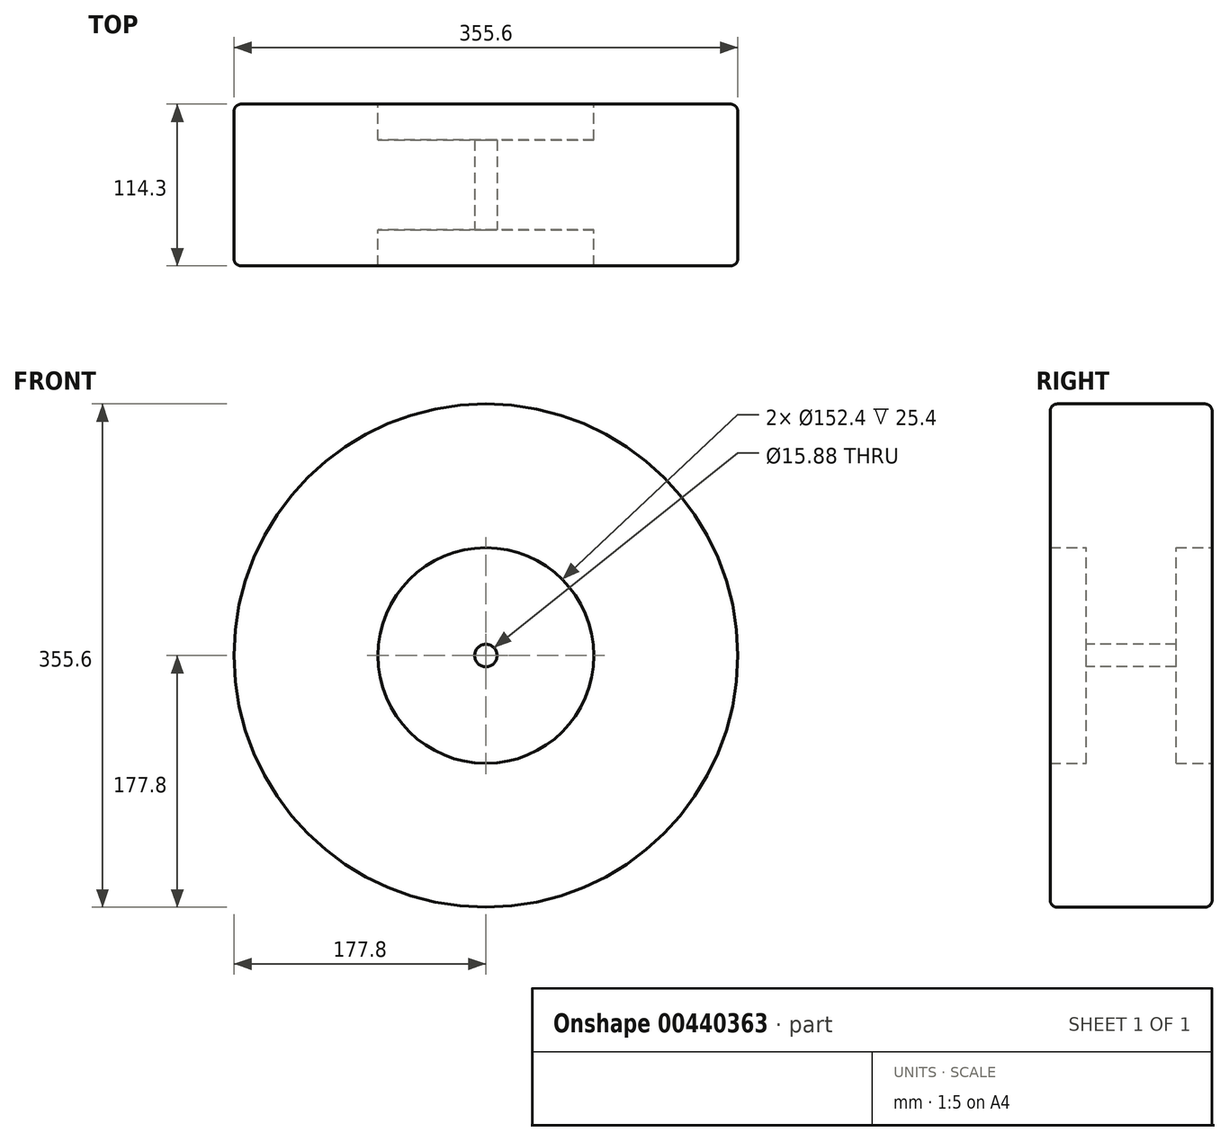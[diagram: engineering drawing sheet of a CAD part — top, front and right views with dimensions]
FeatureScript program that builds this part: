
annotation { "Feature Type Name" : "Feature", "Feature Type Description" : "" }
export const myFeature = defineFeature(function(context is Context, id is Id, definition is map)
    precondition{}
    {
        {
            var Q0;
            Q0=qCreatedBy(makeId("Front.planeOp"),FACE);
            var sketch = newSketch(context, id + "F0", { "sketchPlane" : qUnion([Q0])});
            skCircle(sketch, "E0", {"center": v(0, 0) * mm, "radius": 177.8 * mm});
            skCircle(sketch, "E1", {"center": v(0, 0) * mm, "radius": 76.2 * mm});
            skCircle(sketch, "E2", {"center": v(0, 0) * mm, "radius": 7.94 * mm});
            skSolve(sketch);
        }
        {
            var Q0;
            Q0=makeQuery(id+"F0.imprint","IMPRINT",FACE,{"disambiguationData":[TD([[makeQuery(id+"F0.imprint","IMPRINT",EDGE,{"derivedFrom":sQuery(id+"F0.wireOp",EDGE,"E0")}),1.0]])]});
            extrude(context, id + "F1", {"entities" : qUnion([Q0]), "endBound" : BoundingType.SYMMETRIC, "depth" : 114.3 * mm});
        }
        {
            var Q0;
            Q0=qCreatedBy(makeId("Front.planeOp"),FACE);
            var sketch = newSketch(context, id + "F2", { "sketchPlane" : qUnion([Q0])});
            skCircle(sketch, "E3", {"center": v(0, 0) * mm, "radius": 76.2 * mm});
            skSolve(sketch);
        }
        {
            var Q0;
            Q0=makeQuery(id+"F2.imprint","IMPRINT",FACE,{"disambiguationData":[TD([[makeQuery(id+"F2.imprint","IMPRINT",EDGE,{"derivedFrom":sQuery(id+"F2.wireOp",EDGE,"E3")}),1.0]])]});
            extrude(context, id + "F3", {"entities" : qUnion([Q0]), "operationType" : NewBodyOperationType.ADD, "endBound" : BoundingType.SYMMETRIC, "depth" : 63.5 * mm});
        }
        {
            var Q0;
            Q0=makeQuery(id+"F3.opExtrude","CAP_FACE",FACE,{"disambiguationData":[OSD([sQuery(id+"F2.wireOp",EDGE,"E3")])],"isStart":false});
            var sketch = newSketch(context, id + "F4", { "sketchPlane" : qUnion([Q0])});
            skCircle(sketch, "E4", {"center": v(0, 0) * mm, "radius": 7.94 * mm});
            skSolve(sketch);
        }
        {
            var Q0;
            Q0=makeQuery(id+"F4.imprint","IMPRINT",FACE,{"disambiguationData":[TD([[makeQuery(id+"F4.imprint","IMPRINT",EDGE,{"derivedFrom":sQuery(id+"F4.wireOp",EDGE,"E4")}),1.0]])]});
            extrude(context, id + "F5", {"entities" : qUnion([Q0]), "operationType" : NewBodyOperationType.REMOVE, "endBound" : BoundingType.SYMMETRIC, "oppositeDirection" : true, "depth" : 127 * mm});
        }
        {
            var Q0;
            Q0=makeQuery(id+"F1.opExtrude","CAP_EDGE",EDGE,{"disambiguationData":[OSD([sQuery(id+"F0.wireOp",EDGE,"E0")])],"isStart":false});
            var Q1;
            Q1=makeQuery(id+"F1.opExtrude","CAP_EDGE",EDGE,{"disambiguationData":[OSD([sQuery(id+"F0.wireOp",EDGE,"E0")])],"isStart":true});
            fillet(context, id + "F6", {"entities" : qUnion([Q0, Q1]), "radius" : 5.08 * mm, "tangentPropagation" : true, "allowEdgeOverflow" : false});
        }
    });
